# Revit family: Interceptor_Sand-Zurn-Z1187-SI
name_source: partatom
category: Plumbing Fixtures
units: mm (PartAtom-declared; Revit-internal decimal feet)

## family parameters
Always vertical = Yes
Cut with Voids When Loaded = No
Maintain Annotation Orientation = No
OmniClass Number = 23.45.55.21
OmniClass Title = Drains (Wastes)
Part Type = Normal
Room Calculation Point = No
Round Connector Dimension = Use Radius
Shared = No
Work Plane-Based = No

## types (5) — shared parameters
Assembly Code = D2090300
Body Offset = 0.5 "
Body Side offset_1 = 1.5 "
CW Connection = No
Default Elevation = 48 "
Description = SAND INTERCEPTOR
End to Side Wall Distance = 2.875 "
HW Connection = No
Main Material = Steel - Zurn - Fabricated - Acid resistant Coated
Manufacturer = Zurn Water, LLC
Manufacurer Brand = Zurn
Model = Z1187-SI
Modified Date = 02/06/2026
Outlet Distance = 1.25 "
Product Documentation Link = https://files.zurn.com
Product Page URL = https://www.zurn.com
Product data url = https://www.bimobject.com
URL = www.zurn.com
Vent Connection = No
WFU = 1
Waste Connection = Yes
zero-valued in all types: CWFU, HWFU

## per-type parameters (varying)
| type | Approx. Weight (Lbs) | Capacity Gal. (L) | Dimension D | Dimension L | Flow G.P.M. (L) | Length L' | No. of Grates | Pipe Size_A Inside Radius | Pipe Size_A Nominal Radius | Pipe Size_A Outer Radius | Side Distance | Visibility_Size150 | Visibility_Size20 | Visibility_Size250 | Visibility_Size50 | Visibility_Size500 | Void Length | Width |
| Z1187-SI-20-4 | 133.00 lb | 60.00 L | 26 " | 24 " | 20.00 L | 25.75 " | 2 " | 2.013 " | 2 " | 2.25 " | 1.5 " | No | Yes | No | No | No | 24.25 " | 24 " |
| Z1187-SI-150-4 | 368.00 lb | 360.00 L | 38 " | 48 " | 150.00 L | 49.75 " | 8 " | 2.013 " | 2 " | 2.25 " | 1.5 " | Yes | No | No | No | No | 48.25 " | 48 " |
| Z1187-SI-50-4 | 204.00 lb | 120.00 L | 26 " | 48 " | 50.00 L | 49.75 " | 4 " | 2.013 " | 2 " | 2.25 " | 1.5 " | No | No | No | Yes | No | 48.25 " | 24 " |
| Z1187-SI-250-6 | 1294.00 lb | 540.00 L | 39 " | 72 " | 250.00 L | 73.75 " | 12 " | 3.033 " | 3 " | 3.313 " | 1.5 " | No | No | Yes | No | No | 72.25 " | 48 " |
| Z1187-SI-500-6 | 2204.00 lb | 1200.00 L | 51 " | 120 " | 500.00 L | 121.75 " | 20 " | 3.033 " | 3 " | 3.313 " | 1.625 " | No | No | No | No | Yes | 120.25 " | 48 " |

## geometry (parser evidence)
native form markers: Blend x8, Sweep x20
no freeform markers — native parametric forms only
